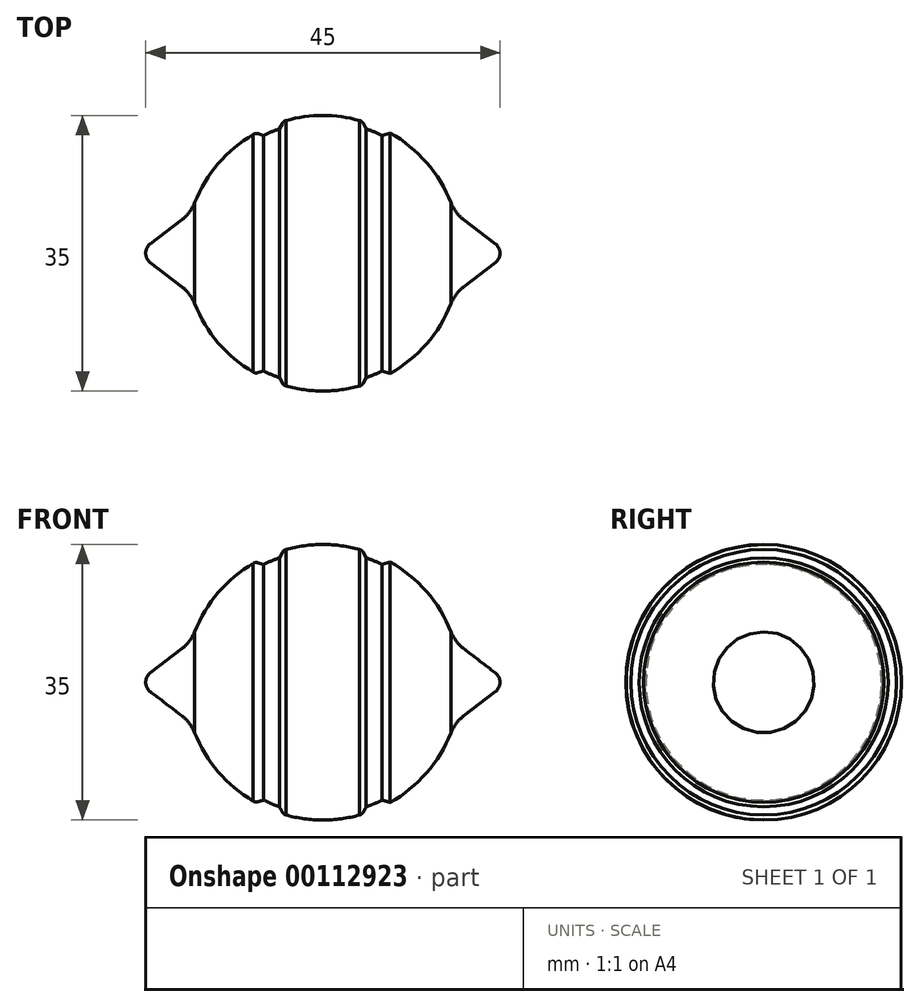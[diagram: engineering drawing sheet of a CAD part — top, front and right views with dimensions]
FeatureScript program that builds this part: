
annotation { "Feature Type Name" : "Feature", "Feature Type Description" : "" }
export const myFeature = defineFeature(function(context is Context, id is Id, definition is map)
    precondition{}
    {
        {
            var Q0;
            Q0=qCreatedBy(makeId("Front.planeOp"),FACE);
            var sketch = newSketch(context, id + "F0", { "sketchPlane" : qUnion([Q0])});
            skLineSegment(sketch, "E0", {"start": v(-69.26, 0) * mm, "end": v(83.25, 0) * mm, "construction": true});
            skSolve(sketch);
        }
        {
            var Q0;
            Q0=qCreatedBy(makeId("Front.planeOp"),FACE);
            var sketch = newSketch(context, id + "F1", { "sketchPlane" : qUnion([Q0])});
            skLineSegment(sketch, "E1", {"start": v(0, -17.5) * mm, "end": v(0, 17.5) * mm});
            skArc(sketch, "E2", {"start": v(0, 17.5) * mm, "mid": v(-17.5, 0) * mm, "end": v(0, -17.5) * mm});
            skSolve(sketch);
        }
        {
            var Q0;
            Q0=makeQuery(id+"F1.imprint","IMPRINT",FACE,{"disambiguationData":[TD([[makeQuery(id+"F1.imprint","IMPRINT",EDGE,{"derivedFrom":sQuery(id+"F1.wireOp",EDGE,"E1")}),1.0]])]});
            var Q1;
            Q1=sQuery(id+"F1.wireOp",EDGE,"E1");
            revolve(context, id + "F2", {"entities" : qUnion([Q0]), "axis" : qUnion([Q1]), "revolveType" : RevolveType.FULL});
        }
        {
            var Q0;
            Q0=qCreatedBy(makeId("Front.planeOp"),FACE);
            var sketch = newSketch(context, id + "F3", { "sketchPlane" : qUnion([Q0])});
            skLineSegment(sketch, "E3", {"start": v(-16.72, 5.18) * mm, "end": v(-23.46, 0) * mm});
            skLineSegment(sketch, "E4", {"start": v(-23.46, 0) * mm, "end": v(-16.72, -5.18) * mm});
            skLineSegment(sketch, "E5", {"start": v(-16.72, -5.18) * mm, "end": v(-16.72, 5.18) * mm});
            skLineSegment(sketch, "E6", {"start": v(-23.46, 0) * mm, "end": v(-16.72, 0) * mm});
            skArc(sketch, "E7", {"start": v(-21.91, 1.2) * mm, "mid": v(-22.5, 0) * mm, "end": v(-21.91, -1.2) * mm});
            skSolve(sketch);
        }
        {
            var Q0;
            {var subQ0=sQuery(id+"F3.wireOp",EDGE,"E5");var subQ1=sQuery(id+"F3.wireOp",EDGE,"E3");var subQ2=makeQuery(id+"F3.imprint","INTERSECT",VERTEX,{"derivedFrom":[subQ1,subQ0]});Q0=makeQuery(id+"F3.imprint","IMPRINT",FACE,{"disambiguationData":[TD([[makeQuery(id+"F3.imprint","IMPRINT",EDGE,{"disambiguationData":[TD([[subQ2,-1.0]])],"derivedFrom":subQ1}),1.0]])]});}
            var Q1;
            Q1=sQuery(id+"F3.wireOp",EDGE,"E6");
            revolve(context, id + "F4", {"entities" : qUnion([Q0]), "axis" : qUnion([Q1]), "revolveType" : RevolveType.FULL});
        }
        {
            var Q0;
            Q0=makeQuery(id+"F4.opRevolve","SWEPT_BODY",BODY,{"disambiguationData":[OSD([sQuery(id+"F3.wireOp",EDGE,"E3"),sQuery(id+"F3.wireOp",EDGE,"E5"),sQuery(id+"F3.wireOp",EDGE,"E6"),sQuery(id+"F3.wireOp",EDGE,"E7")])]});
            var Q1;
            Q1=qCreatedBy(makeId("Right.planeOp"),FACE);
            mirror(context, id + "F5", {"operationType" : NewBodyOperationType.ADD, "entities" : qUnion([Q0]), "mirrorPlane" : qUnion([Q1])});
        }
        {
            var Q0;
            Q0=makeQuery(id+"F2.opRevolve","SWEPT_FACE",FACE,{"disambiguationData":[OSD([sQuery(id+"F1.wireOp",EDGE,"E2")])]});
            fillet(context, id + "F6", {"entities" : qUnion([Q0]), "radius" : 5 * mm, "tangentPropagation" : true, "rho" : 0.5, "crossSection" : FilletCrossSection.CONIC, "allowEdgeOverflow" : false});
        }
        {
            var Q0;
            Q0=qCreatedBy(makeId("Front.planeOp"),FACE);
            var sketch = newSketch(context, id + "F7", { "sketchPlane" : qUnion([Q0])});
            skLineSegment(sketch, "E8", {"start": v(-8.56, 15.26) * mm, "end": v(-7.52, 14.97) * mm});
            skLineSegment(sketch, "E9", {"start": v(-5, 16.77) * mm, "end": v(-5.52, 15.82) * mm});
            skArc(sketch, "E10.0", {"start": v(-5.52, 15.82) * mm, "mid": v(-6.53, 15.42) * mm, "end": v(-7.52, 14.97) * mm});
            skLineSegment(sketch, "E11.0", {"start": v(0, -17.5) * mm, "end": v(0, 17.5) * mm, "construction": true});
            skLineSegment(sketch, "E12", {"start": v(-6.63, 14.25) * mm, "end": v(-6.63, 19.2) * mm, "construction": true});
            skLineSegment(sketch, "E13", {"start": v(-5, 16.77) * mm, "end": v(-2.72, 17.45) * mm, "construction": true});
            skLineSegment(sketch, "E14", {"start": v(-8.56, 15.26) * mm, "end": v(-10, 14.45) * mm, "construction": true});
            skArc(sketch, "E15.0", {"start": v(-5, 16.77) * mm, "mid": v(-6.82, 16.12) * mm, "end": v(-8.56, 15.26) * mm});
            skPoint(sketch, "E16.orphan", {"position": v(0, -17.5) * mm});
            skPoint(sketch, "E17.orphan", {"position": v(0, 17.5) * mm});
            skSolve(sketch);
        }
        {
            var Q0;
            Q0=qSketchRegion(id+"F7",true);
            var Q1;
            Q1=sQuery(id+"F0.wireOp",EDGE,"E0");
            revolve(context, id + "F8", {"entities" : qUnion([Q0]), "axis" : qUnion([Q1]), "revolveType" : RevolveType.FULL, "oppositeDirection" : true});
        }
        {
            var Q0;
            Q0=makeQuery(id+"F8.opRevolve","SWEPT_BODY",BODY,{"disambiguationData":[OSD([sQuery(id+"F7.wireOp",EDGE,"E8"),sQuery(id+"F7.wireOp",EDGE,"E9"),sQuery(id+"F7.wireOp",EDGE,"E10.0"),sQuery(id+"F7.wireOp",EDGE,"E15.0")])]});
            var Q1;
            Q1=qCreatedBy(makeId("Right.planeOp"),FACE);
            mirror(context, id + "F9", {"entities" : qUnion([Q0]), "mirrorPlane" : qUnion([Q1])});
        }
        {
            var Q0;
            Q0=makeQuery(id+"F8.opRevolve","SWEPT_BODY",BODY,{"disambiguationData":[OSD([sQuery(id+"F7.wireOp",EDGE,"E8"),sQuery(id+"F7.wireOp",EDGE,"E9"),sQuery(id+"F7.wireOp",EDGE,"E10.0"),sQuery(id+"F7.wireOp",EDGE,"E15.0")])]});
            var Q1;
            Q1=makeQuery(id+"F9.opPattern","COPY",BODY,{"derivedFrom":makeQuery(id+"F8.opRevolve","SWEPT_BODY",BODY,{"disambiguationData":[OSD([sQuery(id+"F7.wireOp",EDGE,"E8"),sQuery(id+"F7.wireOp",EDGE,"E9"),sQuery(id+"F7.wireOp",EDGE,"E10.0"),sQuery(id+"F7.wireOp",EDGE,"E15.0")])]}),"instanceName":"1"});
            var Q2;
            Q2=makeQuery(id+"F2.opRevolve","SWEPT_BODY",BODY,{"disambiguationData":[OSD([sQuery(id+"F1.wireOp",EDGE,"E1"),sQuery(id+"F1.wireOp",EDGE,"E2")])]});
            booleanBodies(context, id + "F10", {"operationType" : BooleanOperationType.SUBTRACTION, "tools" : qUnion([Q0, Q1]), "targets" : qUnion([Q2])});
        }
        {
            var Q0;
            Q0=makeQuery(id+"F10.opBoolean","COPY",EDGE,{"derivedFrom":makeQuery(id+"F8.opRevolve","SWEPT_EDGE",EDGE,{"disambiguationData":[OSD([sQuery(id+"F7.wireOp",EDGE,"E8"),sQuery(id+"F7.wireOp",EDGE,"E15.0")])]})});
            var Q1;
            Q1=makeQuery(id+"F10.opBoolean","COPY",EDGE,{"derivedFrom":makeQuery(id+"F8.opRevolve","SWEPT_EDGE",EDGE,{"disambiguationData":[OSD([sQuery(id+"F7.wireOp",EDGE,"E9"),sQuery(id+"F7.wireOp",EDGE,"E15.0")])]})});
            var Q2;
            Q2=makeQuery(id+"F10.opBoolean","COPY",EDGE,{"derivedFrom":makeQuery(id+"F9.opPattern","COPY",EDGE,{"derivedFrom":makeQuery(id+"F8.opRevolve","SWEPT_EDGE",EDGE,{"disambiguationData":[OSD([sQuery(id+"F7.wireOp",EDGE,"E9"),sQuery(id+"F7.wireOp",EDGE,"E15.0")])]}),"instanceName":"1"})});
            var Q3;
            Q3=makeQuery(id+"F10.opBoolean","COPY",EDGE,{"derivedFrom":makeQuery(id+"F9.opPattern","COPY",EDGE,{"derivedFrom":makeQuery(id+"F8.opRevolve","SWEPT_EDGE",EDGE,{"disambiguationData":[OSD([sQuery(id+"F7.wireOp",EDGE,"E8"),sQuery(id+"F7.wireOp",EDGE,"E15.0")])]}),"instanceName":"1"})});
            fillet(context, id + "F11", {"entities" : qUnion([Q0, Q1, Q2, Q3]), "radius" : 0.75 * mm, "tangentPropagation" : true, "allowEdgeOverflow" : false});
        }
    });
